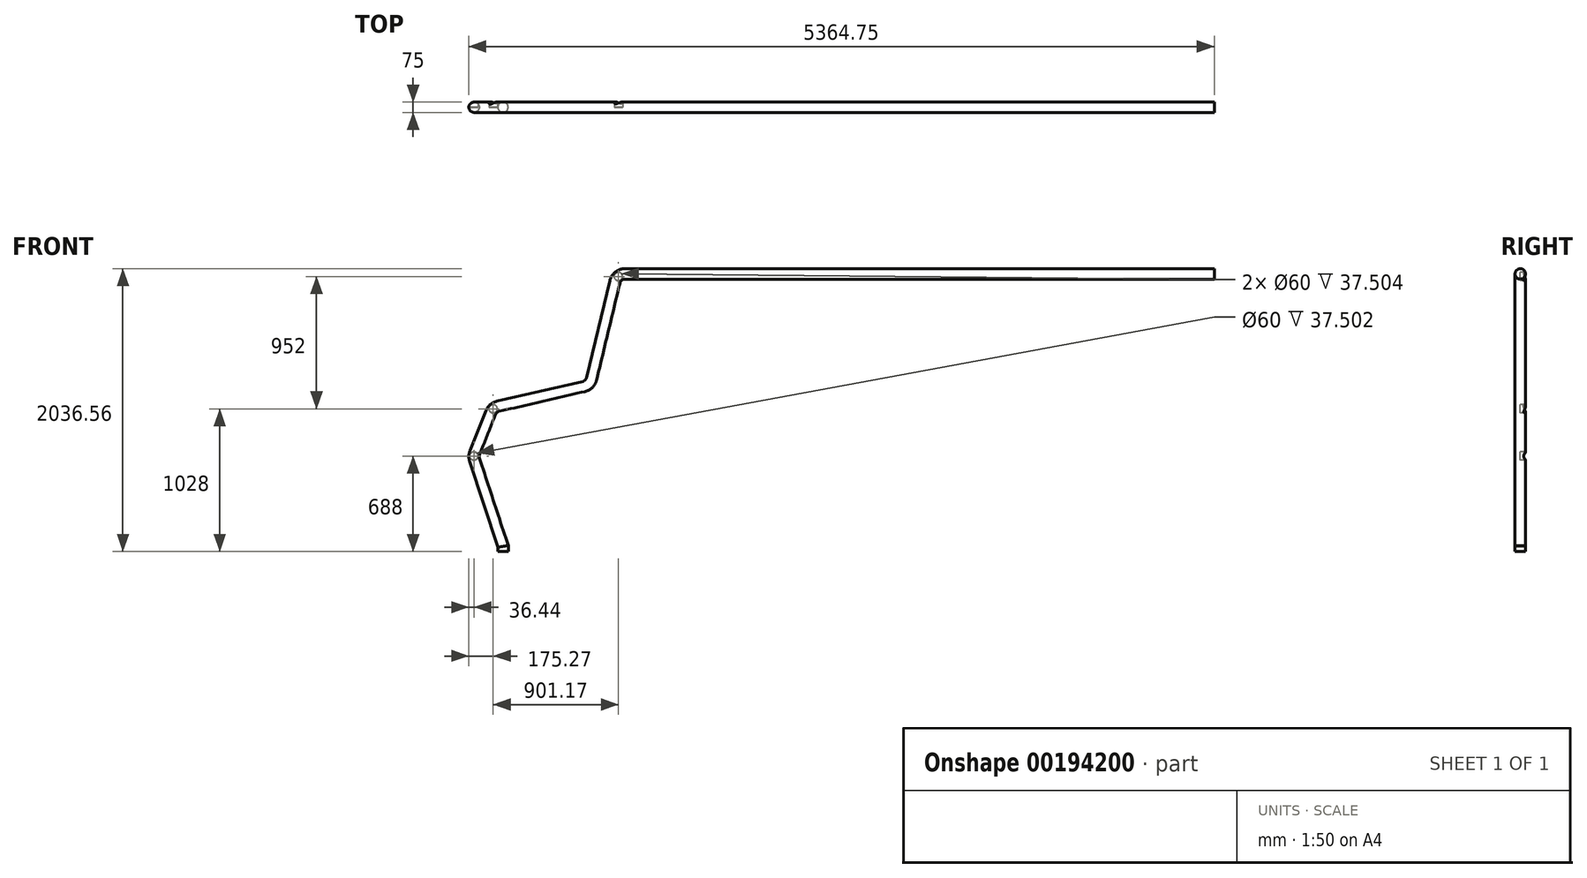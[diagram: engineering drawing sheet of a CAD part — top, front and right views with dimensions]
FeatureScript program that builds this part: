
annotation { "Feature Type Name" : "Feature", "Feature Type Description" : "" }
export const myFeature = defineFeature(function(context is Context, id is Id, definition is map)
    precondition{}
    {
        {
            var Q0;
            Q0=qCreatedBy(makeId("Top.planeOp"),FACE);
            var sketch = newSketch(context, id + "F0", { "sketchPlane" : qUnion([Q0])});
            skCircle(sketch, "E0", {"center": v(0, 0) * mm, "radius": 37.5 * mm});
            skSolve(sketch);
        }
        {
            var Q0;
            Q0=qCreatedBy(makeId("Front.planeOp"),FACE);
            var sketch = newSketch(context, id + "F1", { "sketchPlane" : qUnion([Q0])});
            skLineSegment(sketch, "E1", {"start": v(0, 0) * mm, "end": v(0, 37.5) * mm});
            skLineSegment(sketch, "E2", {"start": v(0, 37.5) * mm, "end": v(-205.18, 661.57) * mm});
            skLineSegment(sketch, "E3", {"start": v(-203.57, 712.85) * mm, "end": v(-88.28, 1001.1) * mm});
            skLineSegment(sketch, "E4", {"start": v(-35.51, 1046.32) * mm, "end": v(581.05, 1188.62) * mm});
            skLineSegment(sketch, "E5", {"start": v(637.12, 1244.2) * mm, "end": v(804.51, 1941.56) * mm});
            skPoint(sketch, "E6.visualSharp", {"position": v(-213.7, 687.5) * mm});
            skArc(sketch, "E6.filletArc", {"start": v(-203.57, 712.85) * mm, "mid": v(-208.9, 687.35) * mm, "end": v(-205.18, 661.57) * mm});
            skPoint(sketch, "E7.visualSharp", {"position": v(-73.72, 1037.5) * mm});
            skArc(sketch, "E7.filletArc", {"start": v(-35.51, 1046.32) * mm, "mid": v(-67.45, 1030.19) * mm, "end": v(-88.28, 1001.1) * mm});
            skPoint(sketch, "E8.visualSharp", {"position": v(626.28, 1199.06) * mm});
            skArc(sketch, "E8.filletArc", {"start": v(581.05, 1188.62) * mm, "mid": v(616.99, 1208.43) * mm, "end": v(637.12, 1244.2) * mm});
            skLineSegment(sketch, "E9", {"start": v(877.44, 1999.06) * mm, "end": v(5118.31, 1999.06) * mm});
            skPoint(sketch, "E10.visualSharp", {"position": v(818.31, 1999.06) * mm});
            skArc(sketch, "E10.filletArc", {"start": v(877.44, 1999.06) * mm, "mid": v(831, 1982.95) * mm, "end": v(804.51, 1941.56) * mm});
            skSolve(sketch);
        }
        {
            var Q0;
            Q0=makeQuery(id+"F0.imprint","IMPRINT",FACE,{"disambiguationData":[TD([[makeQuery(id+"F0.imprint","IMPRINT",EDGE,{"derivedFrom":sQuery(id+"F0.wireOp",EDGE,"E0")}),1.0]])]});
            var Q1;
            Q1=sQuery(id+"F1.wireOp",EDGE,"E1");
            var Q2;
            Q2=sQuery(id+"F1.wireOp",EDGE,"E2");
            var Q3;
            Q3=sQuery(id+"F1.wireOp",EDGE,"E6.filletArc");
            var Q4;
            Q4=sQuery(id+"F1.wireOp",EDGE,"E3");
            var Q5;
            Q5=sQuery(id+"F1.wireOp",EDGE,"E7.filletArc");
            var Q6;
            Q6=sQuery(id+"F1.wireOp",EDGE,"E4");
            var Q7;
            Q7=sQuery(id+"F1.wireOp",EDGE,"E8.filletArc");
            var Q8;
            Q8=sQuery(id+"F1.wireOp",EDGE,"E5");
            var Q9;
            Q9=sQuery(id+"F1.wireOp",EDGE,"E10.filletArc");
            var Q10;
            Q10=sQuery(id+"F1.wireOp",EDGE,"E9");
            sweep(context, id + "F2", {"profiles" : qUnion([Q0]), "path" : qUnion([Q1, Q2, Q3, Q4, Q5, Q6, Q7, Q8, Q9, Q10])});
        }
        {
            var Q0;
            Q0=qCreatedBy(makeId("Front.planeOp"),FACE);
            var sketch = newSketch(context, id + "F3", { "sketchPlane" : qUnion([Q0])});
            skCircle(sketch, "E11", {"center": v(-210, 688) * mm, "radius": 30 * mm});
            skCircle(sketch, "E12", {"center": v(-71.17, 1028) * mm, "radius": 30 * mm});
            skCircle(sketch, "E13", {"center": v(830, 1980) * mm, "radius": 30 * mm});
            skSolve(sketch);
        }
        {
            var Q0;
            Q0 = qSketchRegion(id + "F3", true);
            extrude(context, id + "F4", {"entities" : qUnion([Q0]), "operationType" : NewBodyOperationType.REMOVE, "oppositeDirection" : true, "depth" : 37.5 * mm});
        }
    });
